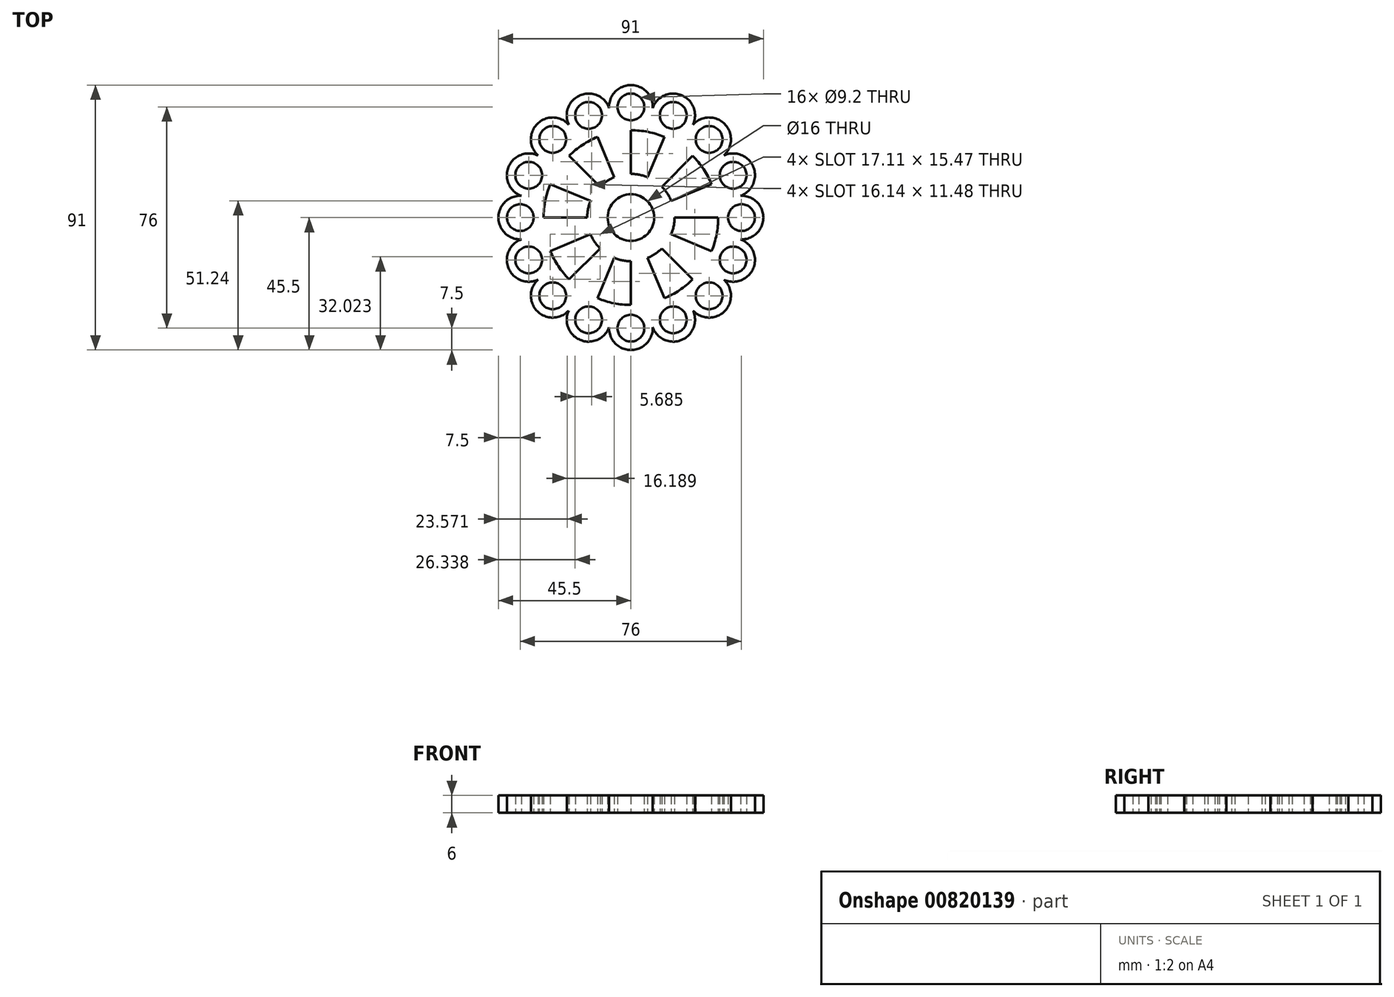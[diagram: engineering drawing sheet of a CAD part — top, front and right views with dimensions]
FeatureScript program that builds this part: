
annotation { "Feature Type Name" : "Feature", "Feature Type Description" : "" }
export const myFeature = defineFeature(function(context is Context, id is Id, definition is map)
    precondition{}
    {
        {
            var Q0;
            Q0=qCreatedBy(makeId("Top.planeOp"),FACE);
            var sketch = newSketch(context, id + "F0", { "sketchPlane" : qUnion([Q0])});
            skCircle(sketch, "E0", {"center": v(0, 38) * mm, "radius": 4.6 * mm});
            skArc(sketch, "E1", {"start": v(7.5, 37.67) * mm, "mid": v(0, 45.5) * mm, "end": v(-7.5, 37.67) * mm});
            skCircle(sketch, "E2.1.1", {"center": v(-14.54, 35.1) * mm, "radius": 4.6 * mm});
            skArc(sketch, "E2.2.0", {"start": v(-21.34, 31.93) * mm, "mid": v(-32.17, 32.17) * mm, "end": v(-31.93, 21.34) * mm});
            skCircle(sketch, "E2.2.1", {"center": v(-26.87, 26.87) * mm, "radius": 4.6 * mm});
            skArc(sketch, "E2.3.0", {"start": v(-31.93, 21.34) * mm, "mid": v(-42.04, 17.41) * mm, "end": v(-37.67, 7.5) * mm});
            skCircle(sketch, "E2.3.1", {"center": v(-35.1, 14.54) * mm, "radius": 4.6 * mm});
            skArc(sketch, "E2.4.0", {"start": v(-37.67, 7.5) * mm, "mid": v(-45.5, 0) * mm, "end": v(-37.67, -7.5) * mm});
            skCircle(sketch, "E2.4.1", {"center": v(-38, 0) * mm, "radius": 4.6 * mm});
            skArc(sketch, "E2.5.0", {"start": v(-37.67, -7.5) * mm, "mid": v(-42.04, -17.41) * mm, "end": v(-31.93, -21.34) * mm});
            skCircle(sketch, "E2.5.1", {"center": v(-35.1, -14.54) * mm, "radius": 4.6 * mm});
            skArc(sketch, "E2.6.0", {"start": v(-31.93, -21.34) * mm, "mid": v(-32.17, -32.17) * mm, "end": v(-21.34, -31.93) * mm});
            skCircle(sketch, "E2.6.1", {"center": v(-26.87, -26.87) * mm, "radius": 4.6 * mm});
            skArc(sketch, "E2.7.0", {"start": v(-21.34, -31.93) * mm, "mid": v(-17.41, -42.04) * mm, "end": v(-7.5, -37.67) * mm});
            skCircle(sketch, "E2.7.1", {"center": v(-14.54, -35.1) * mm, "radius": 4.6 * mm});
            skArc(sketch, "E2.8.0", {"start": v(-7.5, -37.67) * mm, "mid": v(0, -45.5) * mm, "end": v(7.5, -37.67) * mm});
            skCircle(sketch, "E2.8.1", {"center": v(0, -38) * mm, "radius": 4.6 * mm});
            skArc(sketch, "E2.9.0", {"start": v(7.5, -37.67) * mm, "mid": v(17.41, -42.04) * mm, "end": v(21.34, -31.93) * mm});
            skCircle(sketch, "E2.9.1", {"center": v(14.54, -35.1) * mm, "radius": 4.6 * mm});
            skArc(sketch, "E2.10.0", {"start": v(21.34, -31.93) * mm, "mid": v(32.17, -32.17) * mm, "end": v(31.93, -21.34) * mm});
            skCircle(sketch, "E2.10.1", {"center": v(26.87, -26.87) * mm, "radius": 4.6 * mm});
            skArc(sketch, "E2.11.0", {"start": v(31.93, -21.34) * mm, "mid": v(42.04, -17.41) * mm, "end": v(37.67, -7.5) * mm});
            skCircle(sketch, "E2.11.1", {"center": v(35.1, -14.54) * mm, "radius": 4.6 * mm});
            skArc(sketch, "E2.12.0", {"start": v(37.67, -7.5) * mm, "mid": v(45.5, 0) * mm, "end": v(37.67, 7.5) * mm});
            skCircle(sketch, "E2.12.1", {"center": v(38, 0) * mm, "radius": 4.6 * mm});
            skArc(sketch, "E2.13.0", {"start": v(37.67, 7.5) * mm, "mid": v(42.04, 17.41) * mm, "end": v(31.93, 21.34) * mm});
            skCircle(sketch, "E2.13.1", {"center": v(35.1, 14.54) * mm, "radius": 4.6 * mm});
            skArc(sketch, "E2.14.0", {"start": v(31.93, 21.34) * mm, "mid": v(32.17, 32.17) * mm, "end": v(21.34, 31.93) * mm});
            skCircle(sketch, "E2.14.1", {"center": v(26.87, 26.87) * mm, "radius": 4.6 * mm});
            skArc(sketch, "E2.15.0", {"start": v(21.34, 31.93) * mm, "mid": v(17.41, 42.04) * mm, "end": v(7.5, 37.67) * mm});
            skCircle(sketch, "E2.15.1", {"center": v(14.54, 35.1) * mm, "radius": 4.6 * mm});
            skPoint(sketch, "E2.center", {"position": v(0, 0) * mm});
            skArc(sketch, "E3.trimOffspring", {"start": v(-7.5, 37.67) * mm, "mid": v(-17.41, 42.04) * mm, "end": v(-21.34, 31.93) * mm});
            skArc(sketch, "E4", {"start": v(11.48, 27.72) * mm, "mid": v(5.85, 29.42) * mm, "end": v(0, 30) * mm});
            skCircle(sketch, "E5", {"center": v(0, 0) * mm, "radius": 8 * mm});
            skArc(sketch, "E6", {"start": v(5.74, 13.86) * mm, "mid": v(2.93, 14.71) * mm, "end": v(0, 15) * mm});
            skLineSegment(sketch, "E7.trimOffspring", {"start": v(5.74, 13.86) * mm, "end": v(11.48, 27.72) * mm});
            skLineSegment(sketch, "E8.trimOffspring", {"start": v(0, 15) * mm, "end": v(0, 30) * mm});
            skArc(sketch, "E9.1.0", {"start": v(-11.48, 27.72) * mm, "mid": v(-16.67, 24.94) * mm, "end": v(-21.21, 21.21) * mm});
            skLineSegment(sketch, "E9.1.1", {"start": v(-10.6, 10.6) * mm, "end": v(-21.21, 21.21) * mm});
            skLineSegment(sketch, "E9.1.2", {"start": v(-5.74, 13.86) * mm, "end": v(-11.48, 27.72) * mm});
            skArc(sketch, "E9.1.3", {"start": v(-5.74, 13.86) * mm, "mid": v(-8.33, 12.47) * mm, "end": v(-10.6, 10.6) * mm});
            skArc(sketch, "E9.2.0", {"start": v(-27.72, 11.48) * mm, "mid": v(-29.42, 5.85) * mm, "end": v(-30, 0) * mm});
            skLineSegment(sketch, "E9.2.1", {"start": v(-15, 0) * mm, "end": v(-30, 0) * mm});
            skLineSegment(sketch, "E9.2.2", {"start": v(-13.86, 5.74) * mm, "end": v(-27.72, 11.48) * mm});
            skArc(sketch, "E9.2.3", {"start": v(-13.86, 5.74) * mm, "mid": v(-14.71, 2.93) * mm, "end": v(-15, 0) * mm});
            skArc(sketch, "E9.3.0", {"start": v(-27.72, -11.48) * mm, "mid": v(-24.94, -16.67) * mm, "end": v(-21.21, -21.21) * mm});
            skLineSegment(sketch, "E9.3.1", {"start": v(-10.6, -10.6) * mm, "end": v(-21.21, -21.21) * mm});
            skLineSegment(sketch, "E9.3.2", {"start": v(-13.86, -5.74) * mm, "end": v(-27.72, -11.48) * mm});
            skArc(sketch, "E9.3.3", {"start": v(-13.86, -5.74) * mm, "mid": v(-12.47, -8.33) * mm, "end": v(-10.6, -10.6) * mm});
            skArc(sketch, "E9.4.0", {"start": v(-11.48, -27.72) * mm, "mid": v(-5.85, -29.42) * mm, "end": v(0, -30) * mm});
            skLineSegment(sketch, "E9.4.1", {"start": v(0, -15) * mm, "end": v(0, -30) * mm});
            skLineSegment(sketch, "E9.4.2", {"start": v(-5.74, -13.86) * mm, "end": v(-11.48, -27.72) * mm});
            skArc(sketch, "E9.4.3", {"start": v(-5.74, -13.86) * mm, "mid": v(-2.93, -14.71) * mm, "end": v(0, -15) * mm});
            skArc(sketch, "E9.5.0", {"start": v(11.48, -27.72) * mm, "mid": v(16.67, -24.94) * mm, "end": v(21.21, -21.21) * mm});
            skLineSegment(sketch, "E9.5.1", {"start": v(10.6, -10.6) * mm, "end": v(21.21, -21.21) * mm});
            skLineSegment(sketch, "E9.5.2", {"start": v(5.74, -13.86) * mm, "end": v(11.48, -27.72) * mm});
            skArc(sketch, "E9.5.3", {"start": v(5.74, -13.86) * mm, "mid": v(8.33, -12.47) * mm, "end": v(10.6, -10.6) * mm});
            skArc(sketch, "E9.6.0", {"start": v(27.72, -11.48) * mm, "mid": v(29.42, -5.85) * mm, "end": v(30, 0) * mm});
            skLineSegment(sketch, "E9.6.1", {"start": v(15, 0) * mm, "end": v(30, 0) * mm});
            skLineSegment(sketch, "E9.6.2", {"start": v(13.86, -5.74) * mm, "end": v(27.72, -11.48) * mm});
            skArc(sketch, "E9.6.3", {"start": v(13.86, -5.74) * mm, "mid": v(14.71, -2.93) * mm, "end": v(15, 0) * mm});
            skArc(sketch, "E9.7.0", {"start": v(27.72, 11.48) * mm, "mid": v(24.94, 16.67) * mm, "end": v(21.21, 21.21) * mm});
            skLineSegment(sketch, "E9.7.1", {"start": v(10.6, 10.6) * mm, "end": v(21.21, 21.21) * mm});
            skLineSegment(sketch, "E9.7.2", {"start": v(13.86, 5.74) * mm, "end": v(27.72, 11.48) * mm});
            skArc(sketch, "E9.7.3", {"start": v(13.86, 5.74) * mm, "mid": v(12.47, 8.33) * mm, "end": v(10.6, 10.6) * mm});
            skSolve(sketch);
        }
        {
            var Q0;
            Q0 = qSketchRegion(id + "F0", true);
            extrude(context, id + "F1", {"entities" : qUnion([Q0]), "depth" : 6 * mm, "offsetDistance" : 25 * mm});
        }
    });
